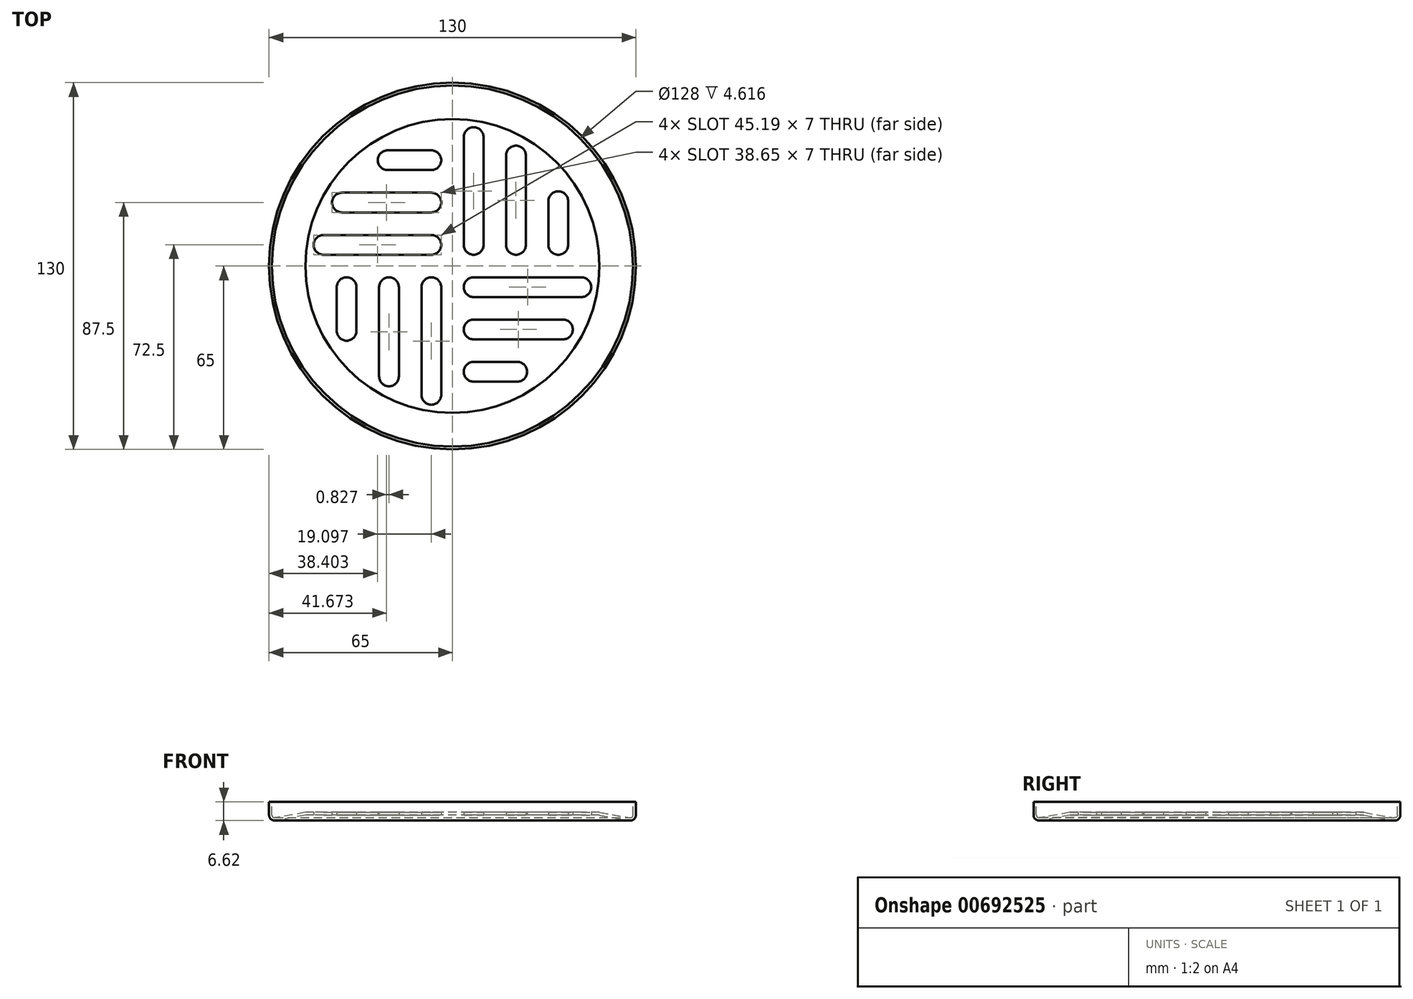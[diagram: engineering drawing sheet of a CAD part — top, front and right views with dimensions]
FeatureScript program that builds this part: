
annotation { "Feature Type Name" : "Feature", "Feature Type Description" : "" }
export const myFeature = defineFeature(function(context is Context, id is Id, definition is map)
    precondition{}
    {
        {
            var Q0;
            Q0=qCreatedBy(makeId("Top.planeOp"),FACE);
            var sketch = newSketch(context, id + "F0", { "sketchPlane" : qUnion([Q0])});
            skLineSegment(sketch, "E0", {"start": v(20.45, 0) * mm, "end": v(50.59, 0) * mm});
            skLineSegment(sketch, "E1", {"start": v(50.59, 0) * mm, "end": v(50.59, 2.78) * mm});
            skLineSegment(sketch, "E2", {"start": v(20.45, 0) * mm, "end": v(20.45, 3.6) * mm});
            skLineSegment(sketch, "E3", {"start": v(20.45, 3.6) * mm, "end": v(16.3, 3.6) * mm});
            skLineSegment(sketch, "E4", {"start": v(16.3, 3.6) * mm, "end": v(16.3, 7.46) * mm});
            skLineSegment(sketch, "E5", {"start": v(16.3, 7.46) * mm, "end": v(12.16, 7.46) * mm});
            skLineSegment(sketch, "E6.0", {"start": v(16.9, 8.06) * mm, "end": v(12.16, 8.06) * mm});
            skLineSegment(sketch, "E6.1", {"start": v(16.9, 4.2) * mm, "end": v(16.9, 8.06) * mm});
            skLineSegment(sketch, "E6.2", {"start": v(49.99, 0.6) * mm, "end": v(49.99, 2.78) * mm});
            skLineSegment(sketch, "E6.3", {"start": v(21.05, 0.6) * mm, "end": v(49.99, 0.6) * mm});
            skLineSegment(sketch, "E6.4", {"start": v(21.05, 0.6) * mm, "end": v(21.05, 4.2) * mm});
            skLineSegment(sketch, "E6.5", {"start": v(21.05, 4.2) * mm, "end": v(16.9, 4.2) * mm});
            skLineSegment(sketch, "E7", {"start": v(12.16, 8.06) * mm, "end": v(12.16, 7.46) * mm});
            skLineSegment(sketch, "E8", {"start": v(49.99, 2.78) * mm, "end": v(50.59, 2.78) * mm});
            skSolve(sketch);
        }
        {
            var Q0;
            Q0=qCreatedBy(makeId("Top.planeOp"),FACE);
            var sketch = newSketch(context, id + "F1", { "sketchPlane" : qUnion([Q0])});
            skLineSegment(sketch, "E9", {"start": v(0, 12.91) * mm, "end": v(0, -2.1) * mm, "construction": true});
            skSolve(sketch);
        }
        {
            var Q0;
            Q0=makeQuery(id+"F0.imprint","IMPRINT",FACE,{"disambiguationData":[TD([[makeQuery(id+"F0.imprint","IMPRINT",EDGE,{"derivedFrom":sQuery(id+"F0.wireOp",EDGE,"E0")}),1.0]])]});
            var Q1;
            Q1=sQuery(id+"F1.wireOp",EDGE,"E9");
            revolve(context, id + "F2", {"entities" : qUnion([Q0]), "axis" : qUnion([Q1]), "revolveType" : RevolveType.FULL});
        }
        {
            var Q0;
            Q0=makeQuery(id+"F2.opRevolve","SWEPT_BODY",BODY,{"disambiguationData":[OSD([sQuery(id+"F0.wireOp",EDGE,"E0"),sQuery(id+"F0.wireOp",EDGE,"E1"),sQuery(id+"F0.wireOp",EDGE,"E2"),sQuery(id+"F0.wireOp",EDGE,"E3"),sQuery(id+"F0.wireOp",EDGE,"E4"),sQuery(id+"F0.wireOp",EDGE,"E5"),sQuery(id+"F0.wireOp",EDGE,"E6.0"),sQuery(id+"F0.wireOp",EDGE,"E6.1"),sQuery(id+"F0.wireOp",EDGE,"E6.2"),sQuery(id+"F0.wireOp",EDGE,"E6.3"),sQuery(id+"F0.wireOp",EDGE,"E6.4"),sQuery(id+"F0.wireOp",EDGE,"E6.5"),sQuery(id+"F0.wireOp",EDGE,"E7"),sQuery(id+"F0.wireOp",EDGE,"E8")])]});
            deleteBodies(context, id + "F3", {"entities" : qUnion([Q0])});
        }
        {
            var Q0;
            Q0=qCreatedBy(makeId("Front.planeOp"),FACE);
            var sketch = newSketch(context, id + "F4", { "sketchPlane" : qUnion([Q0])});
            skLineSegment(sketch, "E10", {"start": v(0, 57.85) * mm, "end": v(0, -62.15) * mm, "construction": true});
            skLineSegment(sketch, "E11", {"start": v(-52, 0) * mm, "end": v(0, 0) * mm});
            skLineSegment(sketch, "E12", {"start": v(-52, 0) * mm, "end": v(-62.65, -1.88) * mm});
            skLineSegment(sketch, "E13", {"start": v(-65, 4.7) * mm, "end": v(-65, 0.1) * mm});
            skPoint(sketch, "E14.visualSharp", {"position": v(-65, -2.3) * mm});
            skArc(sketch, "E14.filletArc", {"start": v(-65, 0.1) * mm, "mid": v(-64.29, -1.44) * mm, "end": v(-62.65, -1.88) * mm});
            skLineSegment(sketch, "E15.0", {"start": v(-52.09, 1) * mm, "end": v(0, 1) * mm});
            skLineSegment(sketch, "E15.1", {"start": v(-52.09, 1) * mm, "end": v(-62.83, -0.9) * mm});
            skLineSegment(sketch, "E15.2", {"start": v(-64, 4.7) * mm, "end": v(-64, 0.1) * mm});
            skPoint(sketch, "E16.visualSharp", {"position": v(-64, -1.1) * mm});
            skArc(sketch, "E16.filletArc", {"start": v(-64, 0.1) * mm, "mid": v(-63.64, -0.67) * mm, "end": v(-62.83, -0.9) * mm});
            skLineSegment(sketch, "E17", {"start": v(-65, 4.7) * mm, "end": v(-64, 4.7) * mm});
            skLineSegment(sketch, "E18", {"start": v(0, 1) * mm, "end": v(0, 0) * mm});
            skSolve(sketch);
        }
        {
            var Q0;
            Q0=qSketchRegion(id+"F4",true);
            var Q1;
            Q1=sQuery(id+"F4.wireOp",EDGE,"E10");
            revolve(context, id + "F5", {"entities" : qUnion([Q0]), "axis" : qUnion([Q1]), "revolveType" : RevolveType.FULL});
        }
        {
            var Q0;
            Q0=makeQuery(id+"F5.opRevolve","SWEPT_FACE",FACE,{"disambiguationData":[OSD([sQuery(id+"F4.wireOp",EDGE,"E11")])]});
            var sketch = newSketch(context, id + "F6", { "sketchPlane" : qUnion([Q0])});
            skLineSegment(sketch, "E19.left", {"start": v(-11, 45.7) * mm, "end": v(-11, 7.5) * mm});
            skLineSegment(sketch, "E19.right", {"start": v(-4, 45.7) * mm, "end": v(-4, 7.5) * mm});
            skLineSegment(sketch, "E20", {"start": v(0, 53.56) * mm, "end": v(0, -45.34) * mm, "construction": true});
            skArc(sketch, "E21", {"start": v(-11, 45.7) * mm, "mid": v(-7.5, 49.2) * mm, "end": v(-4, 45.7) * mm});
            skArc(sketch, "E22", {"start": v(-11, 7.5) * mm, "mid": v(-7.5, 4) * mm, "end": v(-4, 7.5) * mm});
            skLineSegment(sketch, "E23", {"start": v(-6.59, 4.12) * mm, "end": v(-8.41, 4.12) * mm, "construction": true});
            skLineSegment(sketch, "E24.left", {"start": v(-26, 39.15) * mm, "end": v(-26, 7.5) * mm});
            skLineSegment(sketch, "E24.right", {"start": v(-19, 39.15) * mm, "end": v(-19, 7.5) * mm});
            skLineSegment(sketch, "E25.left", {"start": v(-41, 22.98) * mm, "end": v(-41, 7.5) * mm});
            skLineSegment(sketch, "E25.right", {"start": v(-34, 22.98) * mm, "end": v(-34, 7.5) * mm});
            skArc(sketch, "E26", {"start": v(-26, 39.15) * mm, "mid": v(-22.5, 42.65) * mm, "end": v(-19, 39.15) * mm});
            skArc(sketch, "E27", {"start": v(-26, 7.5) * mm, "mid": v(-22.5, 4) * mm, "end": v(-19, 7.5) * mm});
            skArc(sketch, "E28", {"start": v(-34, 22.98) * mm, "mid": v(-37.5, 26.48) * mm, "end": v(-41, 22.98) * mm});
            skArc(sketch, "E29", {"start": v(-34, 7.5) * mm, "mid": v(-37.5, 4) * mm, "end": v(-41, 7.5) * mm});
            skLineSegment(sketch, "E30.trimOffspring", {"start": v(-21.59, 4.12) * mm, "end": v(-23.41, 4.12) * mm, "construction": true});
            skLineSegment(sketch, "E31.trimOffspring", {"start": v(-36.59, 4.12) * mm, "end": v(-38.41, 4.12) * mm, "construction": true});
            skArc(sketch, "E32.1.0", {"start": v(-45.7, -11) * mm, "mid": v(-49.2, -7.5) * mm, "end": v(-45.7, -4) * mm});
            skLineSegment(sketch, "E32.1.1", {"start": v(-45.7, -11) * mm, "end": v(-7.5, -11) * mm});
            skLineSegment(sketch, "E32.1.2", {"start": v(-45.7, -4) * mm, "end": v(-7.5, -4) * mm});
            skArc(sketch, "E32.1.3", {"start": v(-7.5, -11) * mm, "mid": v(-4, -7.5) * mm, "end": v(-7.5, -4) * mm});
            skLineSegment(sketch, "E32.1.4", {"start": v(-39.15, -19) * mm, "end": v(-7.5, -19) * mm});
            skLineSegment(sketch, "E32.1.5", {"start": v(-39.15, -26) * mm, "end": v(-7.5, -26) * mm});
            skArc(sketch, "E32.1.6", {"start": v(-39.15, -26) * mm, "mid": v(-42.65, -22.5) * mm, "end": v(-39.15, -19) * mm});
            skArc(sketch, "E32.1.7", {"start": v(-7.5, -26) * mm, "mid": v(-4, -22.5) * mm, "end": v(-7.5, -19) * mm});
            skLineSegment(sketch, "E32.1.8", {"start": v(-4.12, -36.59) * mm, "end": v(-4.12, -38.41) * mm, "construction": true});
            skLineSegment(sketch, "E32.1.9", {"start": v(-22.98, -34) * mm, "end": v(-7.5, -34) * mm});
            skArc(sketch, "E32.1.10", {"start": v(-7.5, -34) * mm, "mid": v(-4, -37.5) * mm, "end": v(-7.5, -41) * mm});
            skLineSegment(sketch, "E32.1.11", {"start": v(-22.98, -41) * mm, "end": v(-7.5, -41) * mm});
            skArc(sketch, "E32.1.12", {"start": v(-22.98, -34) * mm, "mid": v(-26.48, -37.5) * mm, "end": v(-22.98, -41) * mm});
            skArc(sketch, "E32.2.0", {"start": v(11, -45.7) * mm, "mid": v(7.5, -49.2) * mm, "end": v(4, -45.7) * mm});
            skLineSegment(sketch, "E32.2.1", {"start": v(11, -45.7) * mm, "end": v(11, -7.5) * mm});
            skLineSegment(sketch, "E32.2.2", {"start": v(4, -45.7) * mm, "end": v(4, -7.5) * mm});
            skArc(sketch, "E32.2.3", {"start": v(11, -7.5) * mm, "mid": v(7.5, -4) * mm, "end": v(4, -7.5) * mm});
            skLineSegment(sketch, "E32.2.4", {"start": v(19, -39.15) * mm, "end": v(19, -7.5) * mm});
            skLineSegment(sketch, "E32.2.5", {"start": v(26, -39.15) * mm, "end": v(26, -7.5) * mm});
            skArc(sketch, "E32.2.6", {"start": v(26, -39.15) * mm, "mid": v(22.5, -42.65) * mm, "end": v(19, -39.15) * mm});
            skArc(sketch, "E32.2.7", {"start": v(26, -7.5) * mm, "mid": v(22.5, -4) * mm, "end": v(19, -7.5) * mm});
            skLineSegment(sketch, "E32.2.8", {"start": v(36.59, -4.12) * mm, "end": v(38.41, -4.12) * mm, "construction": true});
            skLineSegment(sketch, "E32.2.9", {"start": v(34, -22.98) * mm, "end": v(34, -7.5) * mm});
            skArc(sketch, "E32.2.10", {"start": v(34, -7.5) * mm, "mid": v(37.5, -4) * mm, "end": v(41, -7.5) * mm});
            skLineSegment(sketch, "E32.2.11", {"start": v(41, -22.98) * mm, "end": v(41, -7.5) * mm});
            skArc(sketch, "E32.2.12", {"start": v(34, -22.98) * mm, "mid": v(37.5, -26.48) * mm, "end": v(41, -22.98) * mm});
            skArc(sketch, "E32.3.0", {"start": v(45.7, 11) * mm, "mid": v(49.2, 7.5) * mm, "end": v(45.7, 4) * mm});
            skLineSegment(sketch, "E32.3.1", {"start": v(45.7, 11) * mm, "end": v(7.5, 11) * mm});
            skLineSegment(sketch, "E32.3.2", {"start": v(45.7, 4) * mm, "end": v(7.5, 4) * mm});
            skArc(sketch, "E32.3.3", {"start": v(7.5, 11) * mm, "mid": v(4, 7.5) * mm, "end": v(7.5, 4) * mm});
            skLineSegment(sketch, "E32.3.4", {"start": v(39.15, 19) * mm, "end": v(7.5, 19) * mm});
            skLineSegment(sketch, "E32.3.5", {"start": v(39.15, 26) * mm, "end": v(7.5, 26) * mm});
            skArc(sketch, "E32.3.6", {"start": v(39.15, 26) * mm, "mid": v(42.65, 22.5) * mm, "end": v(39.15, 19) * mm});
            skArc(sketch, "E32.3.7", {"start": v(7.5, 26) * mm, "mid": v(4, 22.5) * mm, "end": v(7.5, 19) * mm});
            skLineSegment(sketch, "E32.3.8", {"start": v(4.12, 36.59) * mm, "end": v(4.12, 38.41) * mm, "construction": true});
            skLineSegment(sketch, "E32.3.9", {"start": v(22.98, 34) * mm, "end": v(7.5, 34) * mm});
            skArc(sketch, "E32.3.10", {"start": v(7.5, 34) * mm, "mid": v(4, 37.5) * mm, "end": v(7.5, 41) * mm});
            skLineSegment(sketch, "E32.3.11", {"start": v(22.98, 41) * mm, "end": v(7.5, 41) * mm});
            skArc(sketch, "E32.3.12", {"start": v(22.98, 34) * mm, "mid": v(26.48, 37.5) * mm, "end": v(22.98, 41) * mm});
            skPoint(sketch, "E32.center", {"position": v(0, 0) * mm});
            skSolve(sketch);
        }
        {
            var Q0;
            Q0=qSketchRegion(id+"F6",true);
            extrude(context, id + "F7", {"entities" : qUnion([Q0]), "operationType" : NewBodyOperationType.REMOVE, "oppositeDirection" : true, "depth" : 1 * mm});
        }
    });
